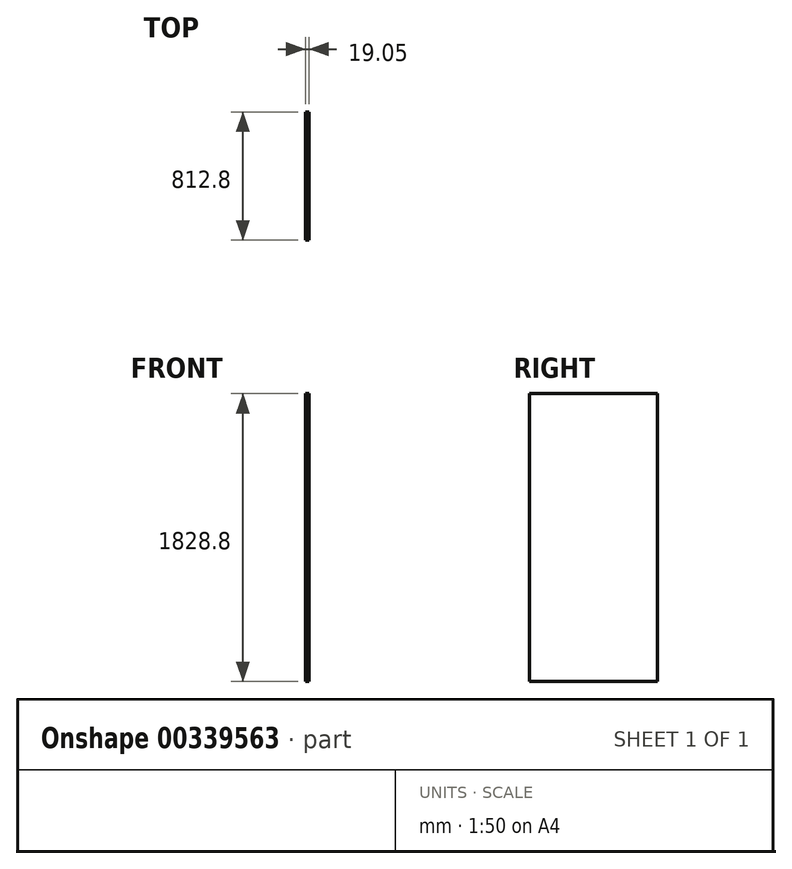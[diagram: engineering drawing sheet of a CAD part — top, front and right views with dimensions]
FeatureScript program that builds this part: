
annotation { "Feature Type Name" : "Feature", "Feature Type Description" : "" }
export const myFeature = defineFeature(function(context is Context, id is Id, definition is map)
    precondition{}
    {
        {
            var Q0;
            Q0=qCreatedBy(makeId("Right.planeOp"),FACE);
            var sketch = newSketch(context, id + "F0", { "sketchPlane" : qUnion([Q0])});
            skLineSegment(sketch, "E0.bottom", {"start": v(406.4, -917.97) * mm, "end": v(-406.4, -917.97) * mm});
            skLineSegment(sketch, "E0.top", {"start": v(406.4, 910.83) * mm, "end": v(-406.4, 910.83) * mm});
            skLineSegment(sketch, "E0.left", {"start": v(406.4, -917.97) * mm, "end": v(406.4, 910.83) * mm});
            skLineSegment(sketch, "E0.right", {"start": v(-406.4, -917.97) * mm, "end": v(-406.4, 910.83) * mm});
            skPoint(sketch, "E0.middle", {"position": v(0, -3.57) * mm});
            skSolve(sketch);
        }
        {
            var Q0;
            Q0 = qSketchRegion(id + "F0", true);
            extrude(context, id + "F1", {"entities" : qUnion([Q0]), "depth" : 19.05 * mm});
        }
    });
